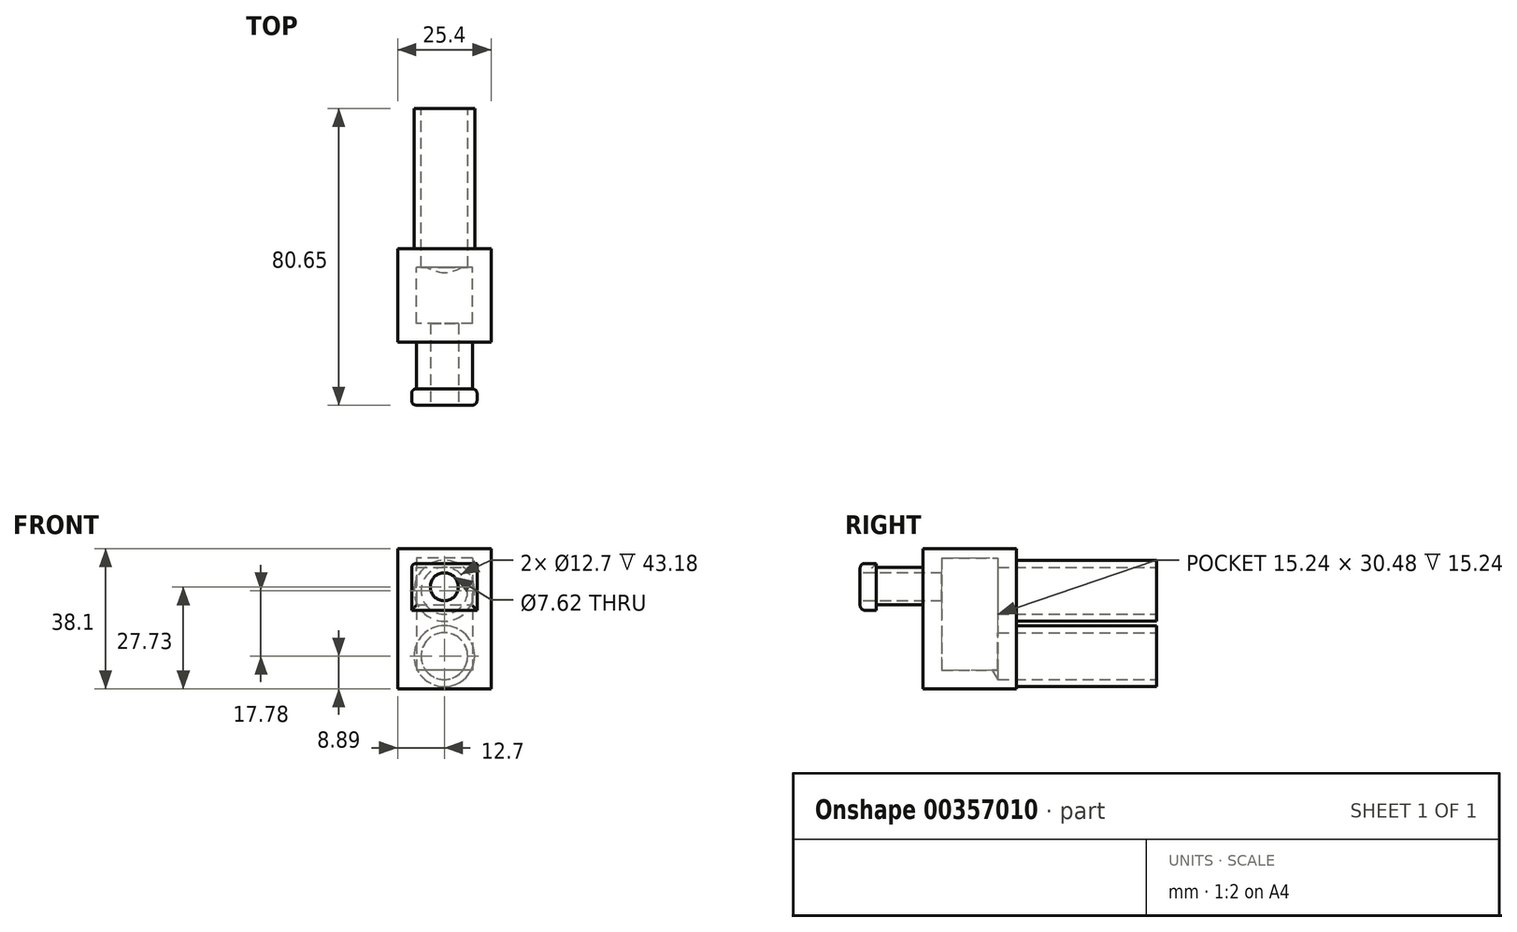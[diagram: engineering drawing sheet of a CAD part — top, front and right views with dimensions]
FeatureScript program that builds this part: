
annotation { "Feature Type Name" : "Feature", "Feature Type Description" : "" }
export const myFeature = defineFeature(function(context is Context, id is Id, definition is map)
    precondition{}
    {
        {
            var Q0;
            Q0=qCreatedBy(makeId("Top.planeOp"),FACE);
            var sketch = newSketch(context, id + "F0", { "sketchPlane" : qUnion([Q0])});
            skLineSegment(sketch, "E0.bottom", {"start": v(12.7, -12.7) * mm, "end": v(-12.7, -12.7) * mm});
            skLineSegment(sketch, "E0.top", {"start": v(12.7, 12.7) * mm, "end": v(-12.7, 12.7) * mm});
            skLineSegment(sketch, "E0.left", {"start": v(12.7, -12.7) * mm, "end": v(12.7, 12.7) * mm});
            skLineSegment(sketch, "E0.right", {"start": v(-12.7, -12.7) * mm, "end": v(-12.7, 12.7) * mm});
            skPoint(sketch, "E0.middle", {"position": v(0, 0) * mm});
            skSolve(sketch);
        }
        {
            var Q0;
            Q0=qSketchRegion(id+"F0",true);
            extrude(context, id + "F1", {"entities" : qUnion([Q0]), "depth" : 35.56 * mm});
        }
        {
            var Q0;
            Q0=makeQuery(id+"F1.opExtrude","CAP_FACE",FACE,{"disambiguationData":[OSD([sQuery(id+"F0.wireOp",EDGE,"E0.bottom"),sQuery(id+"F0.wireOp",EDGE,"E0.top"),sQuery(id+"F0.wireOp",EDGE,"E0.left"),sQuery(id+"F0.wireOp",EDGE,"E0.right")])],"isStart":false});
            shell(context, id + "F2", {"entities" : qUnion([Q0]), "thickness" : 5.08 * mm});
        }
        {
            var Q0;
            Q0=makeQuery(id+"F1.opExtrude","CAP_FACE",FACE,{"disambiguationData":[OSD([sQuery(id+"F0.wireOp",EDGE,"E0.bottom"),sQuery(id+"F0.wireOp",EDGE,"E0.top"),sQuery(id+"F0.wireOp",EDGE,"E0.left"),sQuery(id+"F0.wireOp",EDGE,"E0.right")])],"isStart":false});
            var sketch = newSketch(context, id + "F3", { "sketchPlane" : qUnion([Q0])});
            skLineSegment(sketch, "E1.bottom", {"start": v(12.7, -12.7) * mm, "end": v(-12.7, -12.7) * mm});
            skLineSegment(sketch, "E1.top", {"start": v(12.7, 12.7) * mm, "end": v(-12.7, 12.7) * mm});
            skLineSegment(sketch, "E1.left", {"start": v(12.7, -12.7) * mm, "end": v(12.7, 12.7) * mm});
            skLineSegment(sketch, "E1.right", {"start": v(-12.7, -12.7) * mm, "end": v(-12.7, 12.7) * mm});
            skSolve(sketch);
        }
        {
            var Q0;
            Q0=qSketchRegion(id+"F3",true);
            extrude(context, id + "F4", {"entities" : qUnion([Q0]), "operationType" : NewBodyOperationType.ADD, "depth" : 2.54 * mm});
        }
        {
            var Q0;
            Q0=makeQuery(id+"F4.boolean.opBoolean","MERGE",FACE,{"derivedFrom":[makeQuery(id+"F1.opExtrude","SWEPT_FACE",FACE,{"disambiguationData":[OSD([sQuery(id+"F0.wireOp",EDGE,"E0.top")])]}),makeQuery(id+"F4.opExtrude","SWEPT_FACE",FACE,{"disambiguationData":[OSD([sQuery(id+"F3.wireOp",EDGE,"E1.top")])]})]});
            var sketch = newSketch(context, id + "F5", { "sketchPlane" : qUnion([Q0])});
            skCircle(sketch, "E2", {"center": v(0, 26.67) * mm, "radius": 6.35 * mm});
            skCircle(sketch, "E3", {"center": v(0, 8.9) * mm, "radius": 6.35 * mm});
            skCircle(sketch, "E4", {"center": v(0, 26.67) * mm, "radius": 8.26 * mm});
            skCircle(sketch, "E5", {"center": v(0, 8.9) * mm, "radius": 8.26 * mm});
            skSolve(sketch);
        }
        {
            var Q0;
            Q0=sQuery(id+"F5.wireOp",VERTEX,"E2.center");
            var Q1;
            Q1=sQuery(id+"F5.wireOp",VERTEX,"E3.center");
            var Q2;
            Q2=makeQuery(id+"F1.opExtrude","SWEPT_BODY",BODY,{"disambiguationData":[OSD([sQuery(id+"F0.wireOp",EDGE,"E0.bottom"),sQuery(id+"F0.wireOp",EDGE,"E0.top"),sQuery(id+"F0.wireOp",EDGE,"E0.left"),sQuery(id+"F0.wireOp",EDGE,"E0.right")])]});
            hole(context, id + "F6", {"style" : HoleStyle.SIMPLE, "endStyle" : HoleEndStyle.BLIND, "holeDiameter" : 12.7 * mm, "holeDepth" : 5.08 * mm, "tappedDepth" : 12.7 * mm, "tapClearance" : 3, "locations" : qUnion([Q0, Q1]), "scope" : qUnion([Q2])});
        }
        {
            var Q0;
            Q0=makeQuery(id+"F4.boolean.opBoolean","MERGE",FACE,{"derivedFrom":[makeQuery(id+"F1.opExtrude","SWEPT_FACE",FACE,{"disambiguationData":[OSD([sQuery(id+"F0.wireOp",EDGE,"E0.bottom")])]}),makeQuery(id+"F4.opExtrude","SWEPT_FACE",FACE,{"disambiguationData":[OSD([sQuery(id+"F3.wireOp",EDGE,"E1.bottom")])]})]});
            var sketch = newSketch(context, id + "F7", { "sketchPlane" : qUnion([Q0])});
            skLineSegment(sketch, "E6.bottom", {"start": v(-7.62, 22.86) * mm, "end": v(7.62, 22.86) * mm});
            skLineSegment(sketch, "E6.top", {"start": v(-7.62, 33.02) * mm, "end": v(7.62, 33.02) * mm});
            skLineSegment(sketch, "E6.left", {"start": v(-7.62, 22.86) * mm, "end": v(-7.62, 33.02) * mm});
            skLineSegment(sketch, "E6.right", {"start": v(7.62, 22.86) * mm, "end": v(7.62, 33.02) * mm});
            skPoint(sketch, "E6.middle", {"position": v(0, 27.94) * mm});
            skSolve(sketch);
        }
        {
            var Q0;
            Q0=qSketchRegion(id+"F7",true);
            extrude(context, id + "F8", {"entities" : qUnion([Q0]), "operationType" : NewBodyOperationType.ADD, "depth" : 12.7 * mm});
        }
        {
            var Q0;
            Q0=makeQuery(id+"F8.opExtrude","CAP_FACE",FACE,{"disambiguationData":[OSD([sQuery(id+"F7.wireOp",EDGE,"E6.bottom"),sQuery(id+"F7.wireOp",EDGE,"E6.top"),sQuery(id+"F7.wireOp",EDGE,"E6.left"),sQuery(id+"F7.wireOp",EDGE,"E6.right")])],"isStart":false});
            var sketch = newSketch(context, id + "F9", { "sketchPlane" : qUnion([Q0])});
            skLineSegment(sketch, "E7.bottom", {"start": v(5.92, 24.37) * mm, "end": v(-5.92, 24.37) * mm});
            skLineSegment(sketch, "E7.top", {"start": v(5.92, 31.09) * mm, "end": v(-5.92, 31.09) * mm});
            skLineSegment(sketch, "E7.left", {"start": v(5.92, 24.37) * mm, "end": v(5.92, 31.09) * mm});
            skLineSegment(sketch, "E7.right", {"start": v(-5.92, 24.37) * mm, "end": v(-5.92, 31.09) * mm});
            skPoint(sketch, "E7.middle", {"position": v(0, 27.73) * mm});
            skPoint(sketch, "E7.middle.positionSnap0", {"position": v(0, 33.02) * mm});
            skPoint(sketch, "E7.centerSnap0", {"position": v(0, 33.02) * mm});
            skSolve(sketch);
        }
        {
            var Q0;
            Q0=sQuery(id+"F9.wireOp",VERTEX,"E7.middle");
            var Q1;
            Q1=makeQuery(id+"F1.opExtrude","SWEPT_BODY",BODY,{"disambiguationData":[OSD([sQuery(id+"F0.wireOp",EDGE,"E0.bottom"),sQuery(id+"F0.wireOp",EDGE,"E0.top"),sQuery(id+"F0.wireOp",EDGE,"E0.left"),sQuery(id+"F0.wireOp",EDGE,"E0.right")])]});
            hole(context, id + "F10", {"style" : HoleStyle.SIMPLE, "endStyle" : HoleEndStyle.BLIND, "holeDiameter" : 7.62 * mm, "holeDepth" : 20.32 * mm, "tappedDepth" : 12.7 * mm, "tapClearance" : 3, "locations" : qUnion([Q0]), "scope" : qUnion([Q1])});
        }
        {
            var Q0;
            Q0=makeQuery(id+"F8.opExtrude","CAP_FACE",FACE,{"disambiguationData":[OSD([sQuery(id+"F7.wireOp",EDGE,"E6.bottom"),sQuery(id+"F7.wireOp",EDGE,"E6.top"),sQuery(id+"F7.wireOp",EDGE,"E6.left"),sQuery(id+"F7.wireOp",EDGE,"E6.right")])],"isStart":false});
            var sketch = newSketch(context, id + "F11", { "sketchPlane" : qUnion([Q0])});
            skLineSegment(sketch, "E8.bottom", {"start": v(-8.9, 21.38) * mm, "end": v(8.9, 21.38) * mm});
            skLineSegment(sketch, "E8.top", {"start": v(-8.9, 34.08) * mm, "end": v(8.89, 34.08) * mm});
            skLineSegment(sketch, "E8.left", {"start": v(-8.9, 21.38) * mm, "end": v(-8.9, 34.08) * mm});
            skLineSegment(sketch, "E8.right", {"start": v(8.9, 21.38) * mm, "end": v(8.89, 34.08) * mm});
            skPoint(sketch, "E8.middle", {"position": v(0, 27.73) * mm});
            skSolve(sketch);
        }
        {
            var Q0;
            Q0=qSketchRegion(id+"F11",true);
            extrude(context, id + "F12", {"entities" : qUnion([Q0]), "operationType" : NewBodyOperationType.ADD, "depth" : 4.44 * mm});
        }
        {
            var Q0;
            Q0=makeQuery(id+"F12.opExtrude","CAP_FACE",FACE,{"disambiguationData":[OSD([sQuery(id+"F11.wireOp",EDGE,"E8.bottom"),sQuery(id+"F11.wireOp",EDGE,"E8.top"),sQuery(id+"F11.wireOp",EDGE,"E8.left"),sQuery(id+"F11.wireOp",EDGE,"E8.right")])],"isStart":false});
            var sketch = newSketch(context, id + "F13", { "sketchPlane" : qUnion([Q0])});
            skLineSegment(sketch, "E9.bottom", {"start": v(-5.92, 24.38) * mm, "end": v(5.92, 24.38) * mm});
            skLineSegment(sketch, "E9.top", {"start": v(-5.92, 31.08) * mm, "end": v(5.92, 31.08) * mm});
            skLineSegment(sketch, "E9.left", {"start": v(-5.92, 24.38) * mm, "end": v(-5.92, 31.08) * mm});
            skLineSegment(sketch, "E9.right", {"start": v(5.92, 24.38) * mm, "end": v(5.92, 31.08) * mm});
            skPoint(sketch, "E9.middle", {"position": v(0, 27.73) * mm});
            skPoint(sketch, "E9.middle.positionSnap0", {"position": v(0, 21.38) * mm});
            skPoint(sketch, "E9.middle.positionSnap1", {"position": v(-8.9, 27.73) * mm});
            skPoint(sketch, "E9.centerSnap0", {"position": v(0, 21.38) * mm});
            skPoint(sketch, "E9.centerSnap1", {"position": v(-8.9, 27.73) * mm});
            skSolve(sketch);
        }
        {
            var Q0;
            Q0=sQuery(id+"F13.wireOp",VERTEX,"E9.middle");
            var Q1;
            Q1=makeQuery(id+"F1.opExtrude","SWEPT_BODY",BODY,{"disambiguationData":[OSD([sQuery(id+"F0.wireOp",EDGE,"E0.bottom"),sQuery(id+"F0.wireOp",EDGE,"E0.top"),sQuery(id+"F0.wireOp",EDGE,"E0.left"),sQuery(id+"F0.wireOp",EDGE,"E0.right")])]});
            hole(context, id + "F14", {"style" : HoleStyle.SIMPLE, "endStyle" : HoleEndStyle.BLIND, "holeDiameter" : 7.62 * mm, "holeDepth" : 20.32 * mm, "tappedDepth" : 12.7 * mm, "tapClearance" : 3, "locations" : qUnion([Q0]), "scope" : qUnion([Q1])});
        }
        {
            var Q0;
            Q0=makeQuery(id+"F12.opExtrude","CAP_EDGE",EDGE,{"disambiguationData":[OSD([sQuery(id+"F11.wireOp",EDGE,"E8.top")])],"isStart":false});
            var Q1;
            Q1=makeQuery(id+"F12.opExtrude","SWEPT_EDGE",EDGE,{"disambiguationData":[OSD([sQuery(id+"F11.wireOp",EDGE,"E8.top"),sQuery(id+"F11.wireOp",EDGE,"E8.left")])]});
            var Q2;
            Q2=makeQuery(id+"F12.opExtrude","CAP_EDGE",EDGE,{"disambiguationData":[OSD([sQuery(id+"F11.wireOp",EDGE,"E8.left")])],"isStart":false});
            var Q3;
            Q3=makeQuery(id+"F12.opExtrude","CAP_EDGE",EDGE,{"disambiguationData":[OSD([sQuery(id+"F11.wireOp",EDGE,"E8.left")])],"isStart":true});
            var Q4;
            Q4=makeQuery(id+"F12.opExtrude","CAP_EDGE",EDGE,{"disambiguationData":[OSD([sQuery(id+"F11.wireOp",EDGE,"E8.right")])],"isStart":true});
            var Q5;
            Q5=makeQuery(id+"F12.opExtrude","CAP_EDGE",EDGE,{"disambiguationData":[OSD([sQuery(id+"F11.wireOp",EDGE,"E8.bottom")])],"isStart":false});
            var Q6;
            Q6=makeQuery(id+"F12.opExtrude","CAP_EDGE",EDGE,{"disambiguationData":[OSD([sQuery(id+"F11.wireOp",EDGE,"E8.right")])],"isStart":false});
            fillet(context, id + "F15", {"entities" : qUnion([Q0, Q1, Q2, Q3, Q4, Q5, Q6]), "radius" : 1.27 * mm, "tangentPropagation" : true, "allowEdgeOverflow" : false});
        }
        {
            var Q0;
            Q0=qSketchRegion(id+"F5",true);
            extrude(context, id + "F16", {"entities" : qUnion([Q0]), "operationType" : NewBodyOperationType.ADD, "depth" : 38.1 * mm});
        }
    });
